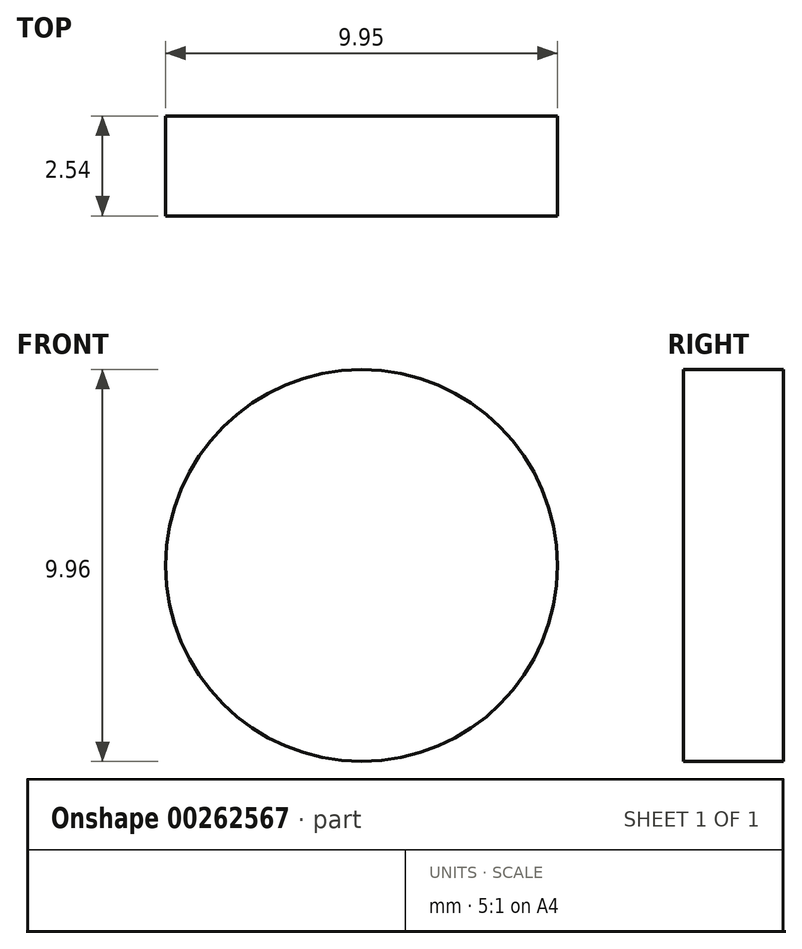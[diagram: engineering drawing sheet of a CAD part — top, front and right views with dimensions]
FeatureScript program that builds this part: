
annotation { "Feature Type Name" : "Feature", "Feature Type Description" : "" }
export const myFeature = defineFeature(function(context is Context, id is Id, definition is map)
    precondition{}
    {
        {
            var Q0;
            Q0=qCreatedBy(makeId("Front.planeOp"),FACE);
            var sketch = newSketch(context, id + "F0", { "sketchPlane" : qUnion([Q0])});
            skCircle(sketch, "E0", {"center": v(-49.8, 48.6) * mm, "radius": 4.98 * mm});
            skSolve(sketch);
        }
        {
            var Q0;
            Q0=makeQuery(id+"F0.imprint","IMPRINT",FACE,{"disambiguationData":[TD([[makeQuery(id+"F0.imprint","IMPRINT",EDGE,{"derivedFrom":sQuery(id+"F0.wireOp",EDGE,"E0")}),1.0]])]});
            extrude(context, id + "F1", {"entities" : qUnion([Q0]), "depth" : 2.54 * mm});
        }
    });
